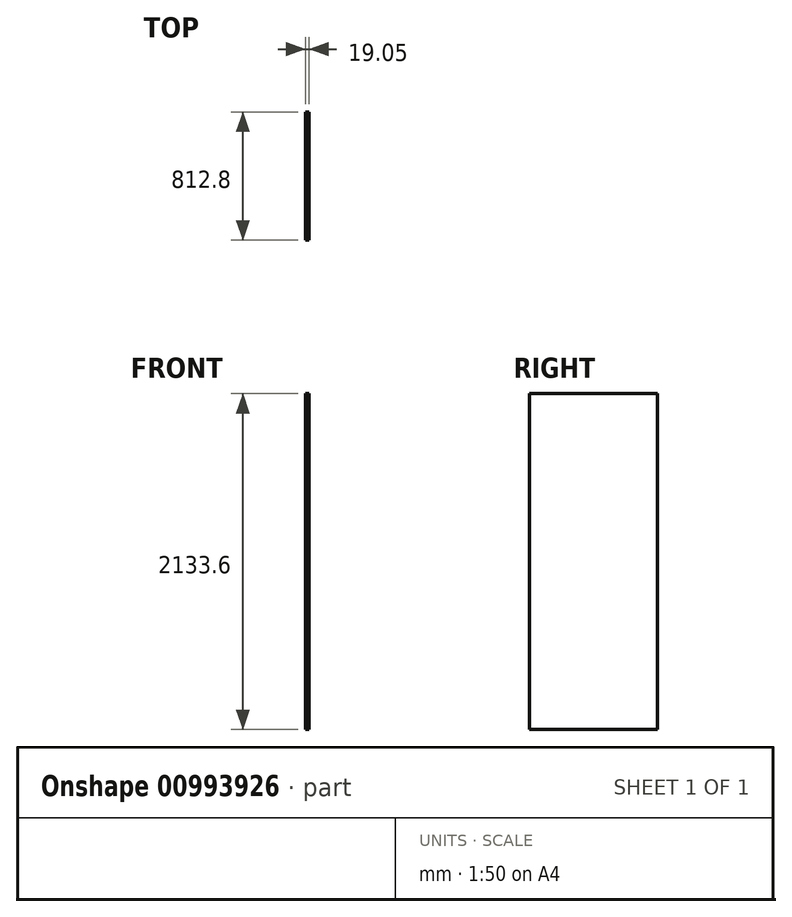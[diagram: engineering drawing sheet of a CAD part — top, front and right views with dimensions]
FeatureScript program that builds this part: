
annotation { "Feature Type Name" : "Feature", "Feature Type Description" : "" }
export const myFeature = defineFeature(function(context is Context, id is Id, definition is map)
    precondition{}
    {
        {
            var Q0;
            Q0=qCreatedBy(makeId("Top.planeOp"),FACE);
            var sketch = newSketch(context, id + "F0", { "sketchPlane" : qUnion([Q0])});
            skLineSegment(sketch, "E0.bottom", {"start": v(0, 0) * mm, "end": v(1193.8, 0) * mm});
            skLineSegment(sketch, "E0.top", {"start": v(0, 2159) * mm, "end": v(1193.8, 2159) * mm});
            skLineSegment(sketch, "E0.left", {"start": v(0, 0) * mm, "end": v(0, 2159) * mm});
            skLineSegment(sketch, "E0.right", {"start": v(1193.8, 0) * mm, "end": v(1193.8, 2159) * mm});
            skSolve(sketch);
        }
        {
            var Q0;
            Q0=makeQuery(id+"F0.imprint","IMPRINT",FACE,{"disambiguationData":[TD([[makeQuery(id+"F0.imprint","IMPRINT",EDGE,{"derivedFrom":sQuery(id+"F0.wireOp",EDGE,"E0.bottom")}),1.0]])]});
            var sketch = newSketch(context, id + "F1", { "sketchPlane" : qUnion([Q0])});
            skLineSegment(sketch, "E1.bottom", {"start": v(0, 0) * mm, "end": v(304.8, 0) * mm});
            skLineSegment(sketch, "E1.top", {"start": v(0, 2159) * mm, "end": v(304.8, 2159) * mm});
            skLineSegment(sketch, "E1.left", {"start": v(0, 0) * mm, "end": v(0, 2159) * mm});
            skLineSegment(sketch, "E1.right", {"start": v(304.8, 0) * mm, "end": v(304.8, 2159) * mm});
            skSolve(sketch);
        }
        {
            var Q0;
            Q0=makeQuery(id+"F0.imprint","IMPRINT",FACE,{"disambiguationData":[TD([[makeQuery(id+"F0.imprint","IMPRINT",EDGE,{"derivedFrom":sQuery(id+"F0.wireOp",EDGE,"E0.bottom")}),1.0]])]});
            var sketch = newSketch(context, id + "F2", { "sketchPlane" : qUnion([Q0])});
            skPoint(sketch, "E2.0", {"position": v(304.8, 0) * mm});
            skLineSegment(sketch, "E3.bottom", {"start": v(304.8, 0) * mm, "end": v(1117.6, 0) * mm});
            skLineSegment(sketch, "E3.top", {"start": v(304.8, 812.8) * mm, "end": v(1117.6, 812.8) * mm});
            skLineSegment(sketch, "E3.left", {"start": v(304.8, 0) * mm, "end": v(304.8, 812.8) * mm});
            skLineSegment(sketch, "E3.right", {"start": v(1117.6, 0) * mm, "end": v(1117.6, 812.8) * mm});
            skSolve(sketch);
        }
        {
            var Q0;
            Q0=makeQuery(id+"F0.imprint","IMPRINT",FACE,{"disambiguationData":[TD([[makeQuery(id+"F0.imprint","IMPRINT",EDGE,{"derivedFrom":sQuery(id+"F0.wireOp",EDGE,"E0.bottom")}),1.0]])]});
            var sketch = newSketch(context, id + "F3", { "sketchPlane" : qUnion([Q0])});
            skPoint(sketch, "E4.0", {"position": v(1117.6, 0) * mm});
            skPoint(sketch, "E5.0", {"position": v(1117.6, 812.8) * mm});
            skLineSegment(sketch, "E6.bottom", {"start": v(1117.6, 0) * mm, "end": v(1136.65, 0) * mm});
            skLineSegment(sketch, "E6.top", {"start": v(1117.6, 812.8) * mm, "end": v(1136.65, 812.8) * mm});
            skLineSegment(sketch, "E6.left", {"start": v(1117.6, 0) * mm, "end": v(1117.6, 812.8) * mm});
            skLineSegment(sketch, "E6.right", {"start": v(1136.65, 0) * mm, "end": v(1136.65, 812.8) * mm});
            skSolve(sketch);
        }
        {
            var Q0;
            Q0=makeQuery(id+"F3.imprint","IMPRINT",FACE,{"disambiguationData":[TD([[makeQuery(id+"F3.imprint","IMPRINT",EDGE,{"derivedFrom":sQuery(id+"F3.wireOp",EDGE,"E6.bottom")}),1.0]])]});
            extrude(context, id + "F4", {"entities" : qUnion([Q0]), "depth" : 2133.6 * mm, "offsetDistance" : 25.4 * mm});
        }
    });
